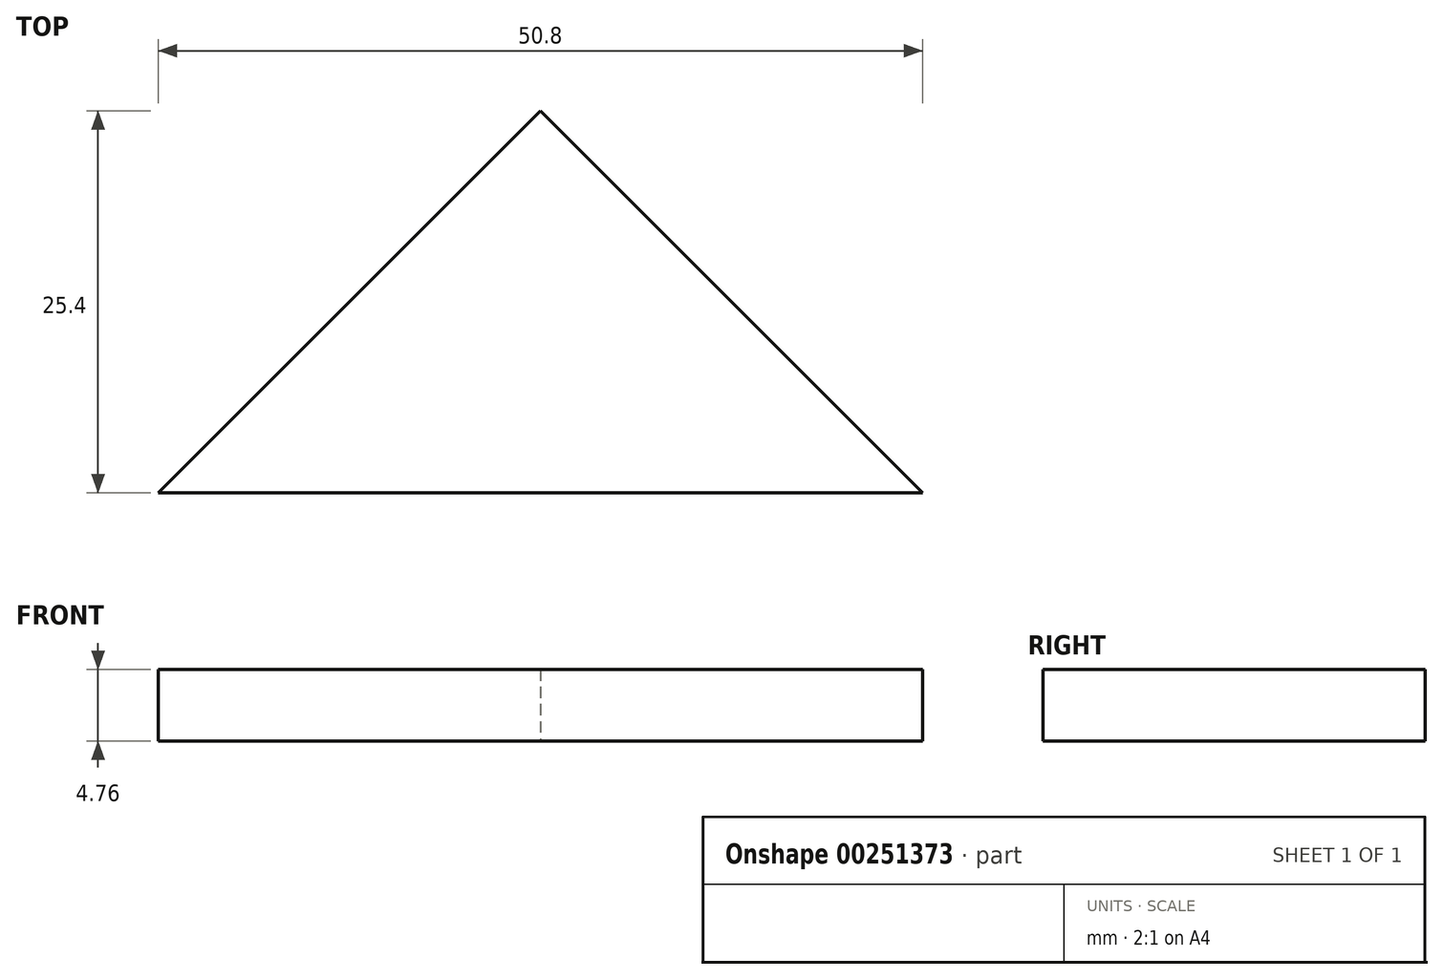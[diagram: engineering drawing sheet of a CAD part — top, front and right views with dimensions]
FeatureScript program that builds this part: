
annotation { "Feature Type Name" : "Feature", "Feature Type Description" : "" }
export const myFeature = defineFeature(function(context is Context, id is Id, definition is map)
    precondition{}
    {
        {
            var Q0;
            Q0=qCreatedBy(makeId("Top.planeOp"),FACE);
            var sketch = newSketch(context, id + "F0", { "sketchPlane" : qUnion([Q0])});
            skLineSegment(sketch, "E0", {"start": v(0, 0) * mm, "end": v(0, 25.4) * mm});
            skLineSegment(sketch, "E1", {"start": v(0, 25.4) * mm, "end": v(-25.4, 0) * mm});
            skLineSegment(sketch, "E2", {"start": v(-25.4, 0) * mm, "end": v(25.4, 0) * mm});
            skLineSegment(sketch, "E3", {"start": v(25.4, 0) * mm, "end": v(0, 25.4) * mm});
            skSolve(sketch);
        }
        {
            var Q0;
            Q0 = qSketchRegion(id + "F0", true);
            extrude(context, id + "F1", {"entities" : qUnion([Q0]), "depth" : 4.76 * mm});
        }
    });
